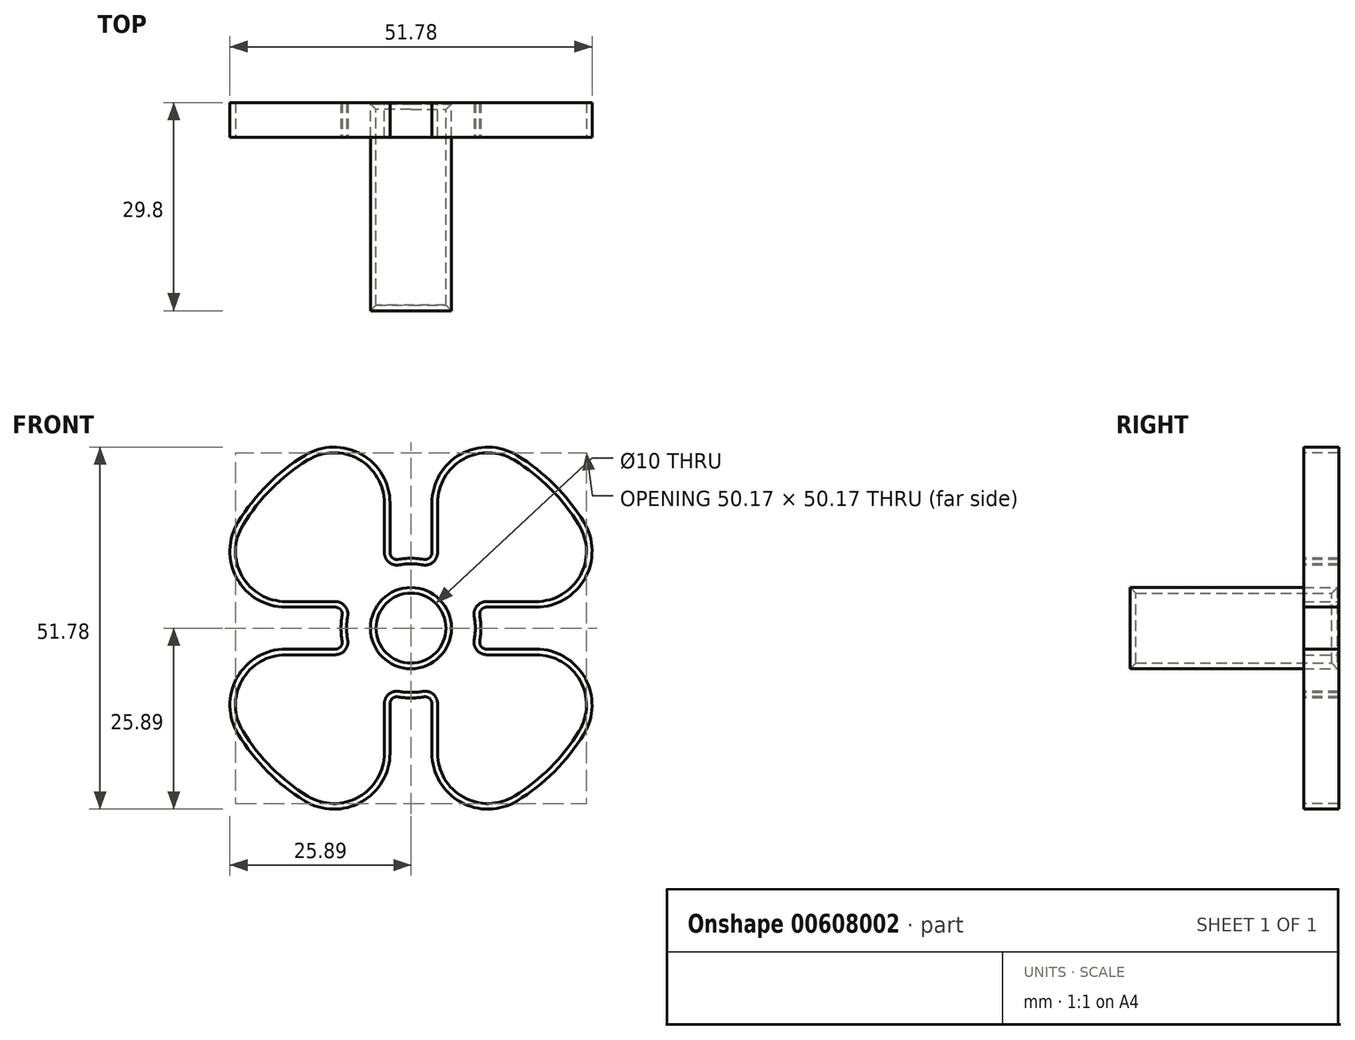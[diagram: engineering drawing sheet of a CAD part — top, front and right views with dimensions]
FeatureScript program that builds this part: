
annotation { "Feature Type Name" : "Feature", "Feature Type Description" : "" }
export const myFeature = defineFeature(function(context is Context, id is Id, definition is map)
    precondition{}
    {
        {
            var Q0;
            Q0=qCreatedBy(makeId("Front.planeOp"),FACE);
            var sketch = newSketch(context, id + "F0", { "sketchPlane" : qUnion([Q0])});
            skCircle(sketch, "E0", {"center": v(0, 0) * mm, "radius": 10 * mm});
            skCircle(sketch, "E1", {"center": v(0, 0) * mm, "radius": 5 * mm});
            skSolve(sketch);
        }
        {
            var Q0;
            Q0=makeQuery(id+"F0.imprint","IMPRINT",FACE,{"disambiguationData":[TD([[makeQuery(id+"F0.imprint","IMPRINT",EDGE,{"derivedFrom":sQuery(id+"F0.wireOp",EDGE,"E0")}),1.0]])]});
            extrude(context, id + "F1", {"entities" : qUnion([Q0]), "depth" : 30 * mm, "offsetDistance" : 25 * mm});
        }
        {
            var Q0;
            Q0=makeQuery(id+"F1.opExtrude","CAP_FACE",FACE,{"disambiguationData":[OSD([sQuery(id+"F0.wireOp",EDGE,"E0"),sQuery(id+"F0.wireOp",EDGE,"E1")])],"isStart":false});
            var sketch = newSketch(context, id + "F2", { "sketchPlane" : qUnion([Q0])});
            skCircle(sketch, "E2", {"center": v(0, 0) * mm, "radius": 29 * mm});
            skSolve(sketch);
        }
        {
            var Q0;
            Q0=makeQuery(id+"F2.imprint","IMPRINT",FACE,{"disambiguationData":[TD([[makeQuery(id+"F2.imprint","IMPRINT",EDGE,{"derivedFrom":sQuery(id+"F2.wireOp",EDGE,"E2")}),1.0]])]});
            var Q1;
            Q1=makeQuery(id+"F1.opExtrude","CAP_FACE",FACE,{"disambiguationData":[OSD([sQuery(id+"F0.wireOp",EDGE,"E0"),sQuery(id+"F0.wireOp",EDGE,"E1")])],"isStart":true});
            extrude(context, id + "F3", {"entities" : qUnion([Q0]), "operationType" : NewBodyOperationType.ADD, "endBound" : BoundingType.UP_TO_SURFACE, "oppositeDirection" : true, "depth" : 25 * mm, "endBoundEntityFace" : qUnion([Q1]), "offsetDistance" : 25 * mm});
        }
        {
            var Q0;
            {var subQ0=sQuery(id+"F0.wireOp",EDGE,"E0");Q0=makeQuery(id+"F3.boolean.opBoolean","MERGE",FACE,{"derivedFrom":[makeQuery(id+"F1.opExtrude","CAP_FACE",FACE,{"disambiguationData":[OSD([subQ0,sQuery(id+"F0.wireOp",EDGE,"E1")])],"isStart":false}),makeQuery(id+"F3.opExtrude","CAP_FACE",FACE,{"disambiguationData":[OSD([subQ0,sQuery(id+"F2.wireOp",EDGE,"E2")])],"isStart":true})]});}
            var sketch = newSketch(context, id + "F4", { "sketchPlane" : qUnion([Q0])});
            skArc(sketch, "E3", {"start": v(-9.54, 3) * mm, "mid": v(-10, 0) * mm, "end": v(-9.54, -3) * mm});
            skLineSegment(sketch, "E4.bottom", {"start": v(3, -33.6) * mm, "end": v(-3, -33.6) * mm});
            skLineSegment(sketch, "E4.top", {"start": v(3, 33.6) * mm, "end": v(-3, 33.6) * mm});
            skLineSegment(sketch, "E4.left", {"start": v(3, -33.6) * mm, "end": v(3, -9.54) * mm});
            skLineSegment(sketch, "E4.right", {"start": v(-3, -33.6) * mm, "end": v(-3, -9.54) * mm});
            skLineSegment(sketch, "E5.bottom", {"start": v(32.17, -3) * mm, "end": v(9.54, -3) * mm});
            skLineSegment(sketch, "E5.top", {"start": v(32.17, 3) * mm, "end": v(9.54, 3) * mm});
            skLineSegment(sketch, "E5.left", {"start": v(32.17, -3) * mm, "end": v(32.17, 3) * mm});
            skLineSegment(sketch, "E5.right", {"start": v(-32.17, -3) * mm, "end": v(-32.17, 3) * mm});
            skLineSegment(sketch, "E6.trimOffspring", {"start": v(-9.54, 3) * mm, "end": v(-32.17, 3) * mm});
            skLineSegment(sketch, "E7.trimOffspring", {"start": v(3, 9.54) * mm, "end": v(3, 33.6) * mm});
            skLineSegment(sketch, "E8.trimOffspring", {"start": v(-3, 9.54) * mm, "end": v(-3, 33.6) * mm});
            skLineSegment(sketch, "E9.trimOffspring", {"start": v(-9.54, -3) * mm, "end": v(-32.17, -3) * mm});
            skArc(sketch, "E10.trimOffspring", {"start": v(3, 9.54) * mm, "mid": v(0, 10) * mm, "end": v(-3, 9.54) * mm});
            skArc(sketch, "E11.trimOffspring", {"start": v(9.54, -3) * mm, "mid": v(10, 0) * mm, "end": v(9.54, 3) * mm});
            skArc(sketch, "E12.trimOffspring", {"start": v(-3, -9.54) * mm, "mid": v(0, -10) * mm, "end": v(3, -9.54) * mm});
            skSolve(sketch);
        }
        {
            var Q0;
            Q0 = qSketchRegion(id + "F4", true);
            extrude(context, id + "F5", {"entities" : qUnion([Q0]), "operationType" : NewBodyOperationType.REMOVE, "endBound" : BoundingType.THROUGH_ALL, "oppositeDirection" : true, "depth" : 25 * mm, "offsetDistance" : 25 * mm});
        }
        {
            var Q0;
            Q0=makeQuery(id+"F5.boolean.opBoolean","INTERSECT",EDGE,{"derivedFrom":[makeQuery(id+"F3.opExtrude","SWEPT_FACE",FACE,{"disambiguationData":[OSD([sQuery(id+"F2.wireOp",EDGE,"E2")])]}),makeQuery(id+"F5.opExtrude","SWEPT_FACE",FACE,{"disambiguationData":[OSD([sQuery(id+"F4.wireOp",EDGE,"E8.trimOffspring")])]})]});
            var Q1;
            Q1=makeQuery(id+"F5.boolean.opBoolean","INTERSECT",EDGE,{"derivedFrom":[makeQuery(id+"F3.opExtrude","SWEPT_FACE",FACE,{"disambiguationData":[OSD([sQuery(id+"F2.wireOp",EDGE,"E2")])]}),makeQuery(id+"F5.opExtrude","SWEPT_FACE",FACE,{"disambiguationData":[OSD([sQuery(id+"F4.wireOp",EDGE,"E6.trimOffspring")])]})]});
            var Q2;
            Q2=makeQuery(id+"F5.boolean.opBoolean","INTERSECT",EDGE,{"derivedFrom":[makeQuery(id+"F3.opExtrude","SWEPT_FACE",FACE,{"disambiguationData":[OSD([sQuery(id+"F2.wireOp",EDGE,"E2")])]}),makeQuery(id+"F5.opExtrude","SWEPT_FACE",FACE,{"disambiguationData":[OSD([sQuery(id+"F4.wireOp",EDGE,"E9.trimOffspring")])]})]});
            var Q3;
            Q3=makeQuery(id+"F5.boolean.opBoolean","INTERSECT",EDGE,{"derivedFrom":[makeQuery(id+"F3.opExtrude","SWEPT_FACE",FACE,{"disambiguationData":[OSD([sQuery(id+"F2.wireOp",EDGE,"E2")])]}),makeQuery(id+"F5.opExtrude","SWEPT_FACE",FACE,{"disambiguationData":[OSD([sQuery(id+"F4.wireOp",EDGE,"E7.trimOffspring")])]})]});
            var Q4;
            Q4=makeQuery(id+"F5.boolean.opBoolean","INTERSECT",EDGE,{"derivedFrom":[makeQuery(id+"F3.opExtrude","SWEPT_FACE",FACE,{"disambiguationData":[OSD([sQuery(id+"F2.wireOp",EDGE,"E2")])]}),makeQuery(id+"F5.opExtrude","SWEPT_FACE",FACE,{"disambiguationData":[OSD([sQuery(id+"F4.wireOp",EDGE,"E4.right")])]})]});
            var Q5;
            Q5=makeQuery(id+"F5.boolean.opBoolean","INTERSECT",EDGE,{"derivedFrom":[makeQuery(id+"F3.opExtrude","SWEPT_FACE",FACE,{"disambiguationData":[OSD([sQuery(id+"F2.wireOp",EDGE,"E2")])]}),makeQuery(id+"F5.opExtrude","SWEPT_FACE",FACE,{"disambiguationData":[OSD([sQuery(id+"F4.wireOp",EDGE,"E4.left")])]})]});
            var Q6;
            Q6=makeQuery(id+"F5.boolean.opBoolean","INTERSECT",EDGE,{"derivedFrom":[makeQuery(id+"F3.opExtrude","SWEPT_FACE",FACE,{"disambiguationData":[OSD([sQuery(id+"F2.wireOp",EDGE,"E2")])]}),makeQuery(id+"F5.opExtrude","SWEPT_FACE",FACE,{"disambiguationData":[OSD([sQuery(id+"F4.wireOp",EDGE,"E5.bottom")])]})]});
            var Q7;
            Q7=makeQuery(id+"F5.boolean.opBoolean","INTERSECT",EDGE,{"derivedFrom":[makeQuery(id+"F3.opExtrude","SWEPT_FACE",FACE,{"disambiguationData":[OSD([sQuery(id+"F2.wireOp",EDGE,"E2")])]}),makeQuery(id+"F5.opExtrude","SWEPT_FACE",FACE,{"disambiguationData":[OSD([sQuery(id+"F4.wireOp",EDGE,"E5.top")])]})]});
            fillet(context, id + "F6", {"entities" : qUnion([Q0, Q1, Q2, Q3, Q4, Q5, Q6, Q7]), "radius" : 8 * mm, "tangentPropagation" : true, "allowEdgeOverflow" : false});
        }
        {
            var Q0;
            Q0=makeQuery(id+"F5.boolean.opBoolean","COPY",EDGE,{"derivedFrom":makeQuery(id+"F5.opExtrude","SWEPT_EDGE",EDGE,{"disambiguationData":[OSD([sQuery(id+"F4.wireOp",EDGE,"E3"),sQuery(id+"F4.wireOp",EDGE,"E6.trimOffspring")])]})});
            var Q1;
            Q1=makeQuery(id+"F5.boolean.opBoolean","COPY",EDGE,{"derivedFrom":makeQuery(id+"F5.opExtrude","SWEPT_EDGE",EDGE,{"disambiguationData":[OSD([sQuery(id+"F4.wireOp",EDGE,"E3"),sQuery(id+"F4.wireOp",EDGE,"E9.trimOffspring")])]})});
            var Q2;
            Q2=makeQuery(id+"F5.boolean.opBoolean","COPY",EDGE,{"derivedFrom":makeQuery(id+"F5.opExtrude","SWEPT_EDGE",EDGE,{"disambiguationData":[OSD([sQuery(id+"F4.wireOp",EDGE,"E4.right"),sQuery(id+"F4.wireOp",EDGE,"E12.trimOffspring")])]})});
            var Q3;
            Q3=makeQuery(id+"F5.boolean.opBoolean","COPY",EDGE,{"derivedFrom":makeQuery(id+"F5.opExtrude","SWEPT_EDGE",EDGE,{"disambiguationData":[OSD([sQuery(id+"F4.wireOp",EDGE,"E4.left"),sQuery(id+"F4.wireOp",EDGE,"E12.trimOffspring")])]})});
            var Q4;
            Q4=makeQuery(id+"F5.boolean.opBoolean","COPY",EDGE,{"derivedFrom":makeQuery(id+"F5.opExtrude","SWEPT_EDGE",EDGE,{"disambiguationData":[OSD([sQuery(id+"F4.wireOp",EDGE,"E5.top"),sQuery(id+"F4.wireOp",EDGE,"E11.trimOffspring")])]})});
            var Q5;
            Q5=makeQuery(id+"F5.boolean.opBoolean","COPY",EDGE,{"derivedFrom":makeQuery(id+"F5.opExtrude","SWEPT_EDGE",EDGE,{"disambiguationData":[OSD([sQuery(id+"F4.wireOp",EDGE,"E5.bottom"),sQuery(id+"F4.wireOp",EDGE,"E11.trimOffspring")])]})});
            var Q6;
            Q6=makeQuery(id+"F5.boolean.opBoolean","COPY",EDGE,{"derivedFrom":makeQuery(id+"F5.opExtrude","SWEPT_EDGE",EDGE,{"disambiguationData":[OSD([sQuery(id+"F4.wireOp",EDGE,"E8.trimOffspring"),sQuery(id+"F4.wireOp",EDGE,"E10.trimOffspring")])]})});
            var Q7;
            Q7=makeQuery(id+"F5.boolean.opBoolean","COPY",EDGE,{"derivedFrom":makeQuery(id+"F5.opExtrude","SWEPT_EDGE",EDGE,{"disambiguationData":[OSD([sQuery(id+"F4.wireOp",EDGE,"E7.trimOffspring"),sQuery(id+"F4.wireOp",EDGE,"E10.trimOffspring")])]})});
            fillet(context, id + "F7", {"entities" : qUnion([Q0, Q1, Q2, Q3, Q4, Q5, Q6, Q7]), "radius" : 1 * mm, "tangentPropagation" : true, "allowEdgeOverflow" : false});
        }
        {
            var Q0;
            {var subQ0=sQuery(id+"F0.wireOp",EDGE,"E0");Q0=makeQuery(id+"F3.boolean.opBoolean","MERGE",FACE,{"derivedFrom":[makeQuery(id+"F1.opExtrude","CAP_FACE",FACE,{"disambiguationData":[OSD([subQ0,sQuery(id+"F0.wireOp",EDGE,"E1")])],"isStart":false}),makeQuery(id+"F3.opExtrude","CAP_FACE",FACE,{"disambiguationData":[OSD([subQ0,sQuery(id+"F2.wireOp",EDGE,"E2")])],"isStart":true})]});}
            shell(context, id + "F8", {"entities" : qUnion([Q0]), "thickness" : 0.8 * mm});
        }
        {
            var Q0;
            Q0=makeQuery(id+"F8.opShell","OFFSET_FACE",FACE,{"disambiguationData":[OSD([sQuery(id+"F0.wireOp",EDGE,"E0"),sQuery(id+"F0.wireOp",EDGE,"E1")]),OD(1.0)]});
            var Q1;
            Q1=makeQuery(id+"F8.opShell","OFFSET_FACE",FACE,{"disambiguationData":[OSD([sQuery(id+"F0.wireOp",EDGE,"E0"),sQuery(id+"F0.wireOp",EDGE,"E1")]),OD(3.0)]});
            var Q2;
            Q2=makeQuery(id+"F8.opShell","OFFSET_FACE",FACE,{"disambiguationData":[OSD([sQuery(id+"F0.wireOp",EDGE,"E0"),sQuery(id+"F0.wireOp",EDGE,"E1")]),OD(2.0)]});
            var Q3;
            Q3=makeQuery(id+"F8.opShell","OFFSET_FACE",FACE,{"disambiguationData":[OSD([sQuery(id+"F0.wireOp",EDGE,"E0"),sQuery(id+"F0.wireOp",EDGE,"E1")]),OD(0.0)]});
            extrude(context, id + "F9", {"entities" : qUnion([Q0, Q1, Q2, Q3]), "operationType" : NewBodyOperationType.REMOVE, "oppositeDirection" : true, "depth" : 25 * mm, "offsetDistance" : 25 * mm});
        }
        {
            var Q0;
            {var subQ0=sQuery(id+"F0.wireOp",EDGE,"E0");Q0=makeQuery(id+"F3.boolean.opBoolean","MERGE",FACE,{"derivedFrom":[makeQuery(id+"F1.opExtrude","CAP_FACE",FACE,{"disambiguationData":[OSD([subQ0,sQuery(id+"F0.wireOp",EDGE,"E1")])],"isStart":false}),makeQuery(id+"F3.opExtrude","CAP_FACE",FACE,{"disambiguationData":[OSD([subQ0,sQuery(id+"F2.wireOp",EDGE,"E2")])],"isStart":true})]});}
            var sketch = newSketch(context, id + "F10", { "sketchPlane" : qUnion([Q0])});
            skCircle(sketch, "E13", {"center": v(0, 0) * mm, "radius": 10 * mm});
            skCircle(sketch, "E14", {"center": v(0, 0) * mm, "radius": 5 * mm});
            skSolve(sketch);
        }
        {
            var Q0;
            Q0=makeQuery(id+"F10.imprint","IMPRINT",FACE,{"disambiguationData":[TD([[makeQuery(id+"F10.imprint","IMPRINT",EDGE,{"derivedFrom":sQuery(id+"F10.wireOp",EDGE,"E14")}),-1.0]])]});
            var Q1;
            {var subQ0=sQuery(id+"F0.wireOp",EDGE,"E1");var subQ1=sQuery(id+"F0.wireOp",EDGE,"E0");Q1=makeQuery(id+"F9.boolean.opBoolean","SPLIT",FACE,{"disambiguationData":[TD([makeQuery(id+"F1.opExtrude","SWEPT_FACE",FACE,{"disambiguationData":[OSD([subQ0])]})])],"derivedFrom":makeQuery(id+"F3.boolean.opBoolean","MERGE",FACE,{"derivedFrom":[makeQuery(id+"F1.opExtrude","CAP_FACE",FACE,{"disambiguationData":[OSD([subQ1,subQ0])],"isStart":true}),makeQuery(id+"F3.opExtrude","CAP_FACE",FACE,{"disambiguationData":[OSD([subQ1,subQ0])],"isStart":false})]})});}
            extrude(context, id + "F11", {"entities" : qUnion([Q0]), "operationType" : NewBodyOperationType.ADD, "endBound" : BoundingType.UP_TO_SURFACE, "oppositeDirection" : true, "depth" : 25 * mm, "endBoundEntityFace" : qUnion([Q1]), "offsetDistance" : 25 * mm});
        }
        {
            var Q0;
            Q0=makeQuery(id+"F1.opExtrude","SWEPT_FACE",FACE,{"disambiguationData":[OSD([sQuery(id+"F0.wireOp",EDGE,"E1")])]});
            chamfer(context, id + "F12", {"entities" : qUnion([Q0]), "width" : 1 * mm, "tangentPropagation" : true});
        }
    });
